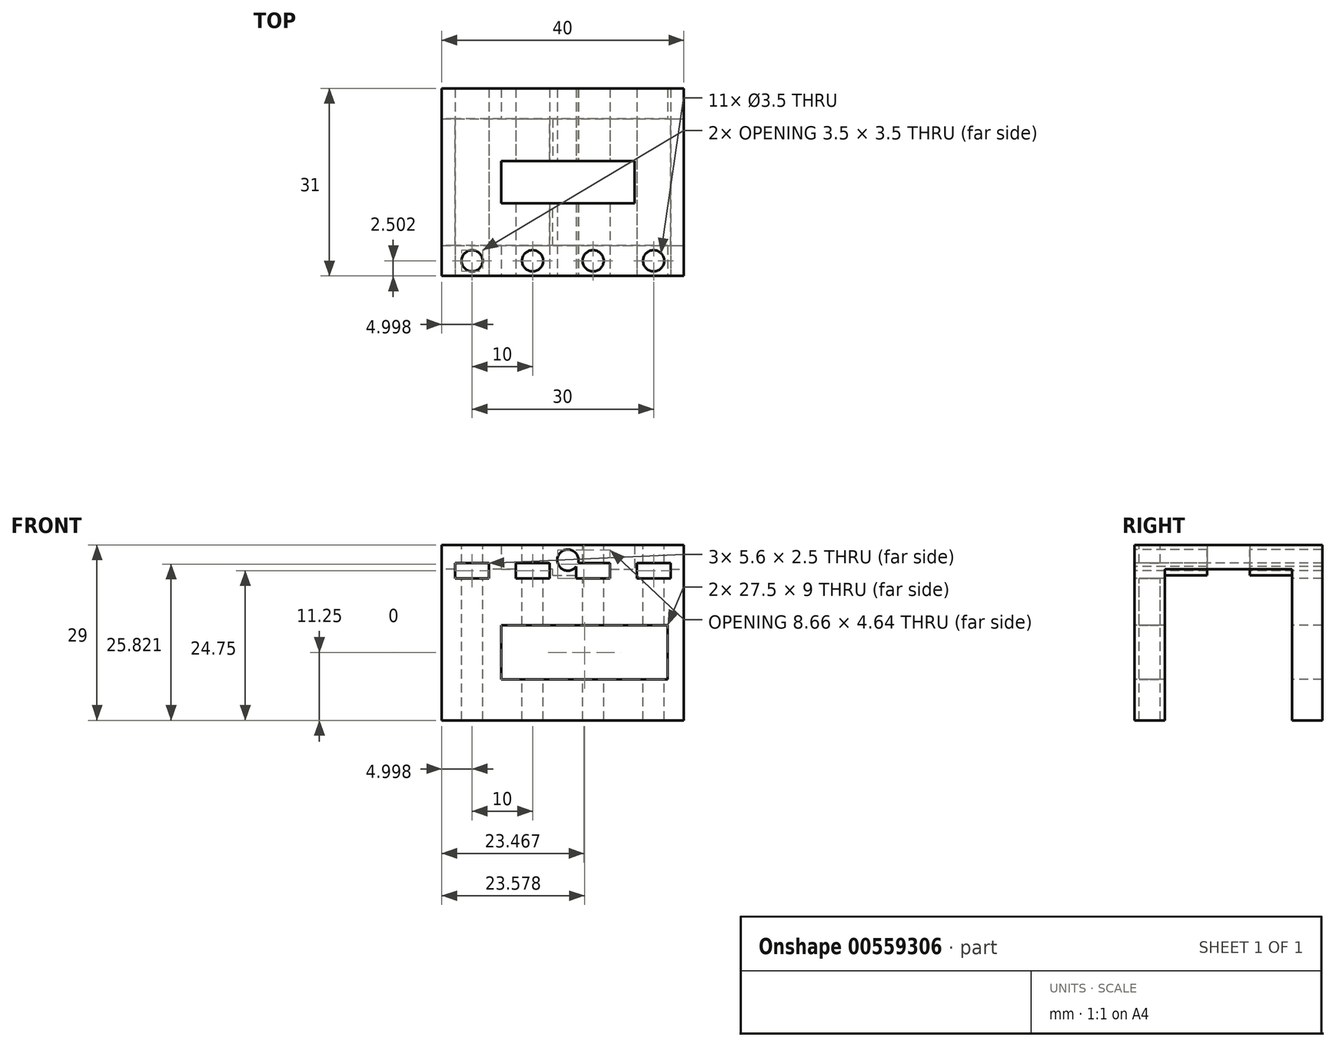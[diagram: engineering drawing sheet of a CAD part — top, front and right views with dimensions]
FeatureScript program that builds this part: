
annotation { "Feature Type Name" : "Feature", "Feature Type Description" : "" }
export const myFeature = defineFeature(function(context is Context, id is Id, definition is map)
    precondition{}
    {
        {
            var Q0;
            Q0=qCreatedBy(makeId("Top.planeOp"),FACE);
            var sketch = newSketch(context, id + "F0", { "sketchPlane" : qUnion([Q0])});
            skLineSegment(sketch, "E0.bottom", {"start": v(-20.38, 4.86) * mm, "end": v(27.96, 4.86) * mm});
            skLineSegment(sketch, "E0.top", {"start": v(-20.38, -15.14) * mm, "end": v(27.96, -15.14) * mm});
            skLineSegment(sketch, "E0.left", {"start": v(-20.38, 4.86) * mm, "end": v(-20.38, -15.14) * mm});
            skLineSegment(sketch, "E0.right", {"start": v(27.96, 4.86) * mm, "end": v(27.96, -15.14) * mm});
            skLineSegment(sketch, "E1.bottom", {"start": v(-7.21, -1.64) * mm, "end": v(14.79, -1.64) * mm});
            skLineSegment(sketch, "E1.top", {"start": v(-7.21, -8.64) * mm, "end": v(14.79, -8.64) * mm});
            skLineSegment(sketch, "E1.left", {"start": v(-7.21, -1.64) * mm, "end": v(-7.21, -8.64) * mm});
            skLineSegment(sketch, "E1.right", {"start": v(14.79, -1.64) * mm, "end": v(14.79, -8.64) * mm});
            skLineSegment(sketch, "E2", {"start": v(3.79, -1.64) * mm, "end": v(3.79, 4.86) * mm, "construction": true});
            skLineSegment(sketch, "E3", {"start": v(3.79, -8.64) * mm, "end": v(3.79, -15.14) * mm, "construction": true});
            skSolve(sketch);
        }
        {
            var Q0;
            Q0=makeQuery(id+"F0.imprint","IMPRINT",FACE,{"disambiguationData":[TD([[makeQuery(id+"F0.imprint","IMPRINT",EDGE,{"derivedFrom":sQuery(id+"F0.wireOp",EDGE,"E0.bottom")}),-1.0]])]});
            extrude(context, id + "F1", {"entities" : qUnion([Q0]), "depth" : 4 * mm, "offsetDistance" : 25 * mm});
        }
        {
            var Q0;
            Q0=makeQuery(id+"F1.opExtrude","CAP_FACE",FACE,{"disambiguationData":[OSD([sQuery(id+"F0.wireOp",EDGE,"E0.bottom"),sQuery(id+"F0.wireOp",EDGE,"E0.top"),sQuery(id+"F0.wireOp",EDGE,"E0.left"),sQuery(id+"F0.wireOp",EDGE,"E0.right"),sQuery(id+"F0.wireOp",EDGE,"E1.bottom"),sQuery(id+"F0.wireOp",EDGE,"E1.top"),sQuery(id+"F0.wireOp",EDGE,"E1.left"),sQuery(id+"F0.wireOp",EDGE,"E1.right")])],"isStart":true});
            var sketch = newSketch(context, id + "F2", { "sketchPlane" : qUnion([Q0])});
            skLineSegment(sketch, "E4", {"start": v(3.79, 8.64) * mm, "end": v(3.79, 1.64) * mm});
            skLineSegment(sketch, "E5", {"start": v(3.79, 8.64) * mm, "end": v(6.29, 8.64) * mm});
            skLineSegment(sketch, "E6", {"start": v(6.29, 8.64) * mm, "end": v(6.29, 15.14) * mm});
            skLineSegment(sketch, "E7", {"start": v(6.29, 15.14) * mm, "end": v(1.29, 15.14) * mm});
            skLineSegment(sketch, "E8", {"start": v(1.29, 15.14) * mm, "end": v(1.29, 8.64) * mm});
            skLineSegment(sketch, "E9", {"start": v(1.29, 8.64) * mm, "end": v(3.79, 8.64) * mm});
            skLineSegment(sketch, "E10", {"start": v(3.79, 1.64) * mm, "end": v(6.29, 1.64) * mm});
            skLineSegment(sketch, "E11", {"start": v(6.29, 1.64) * mm, "end": v(6.29, -4.86) * mm});
            skLineSegment(sketch, "E12", {"start": v(6.29, -4.86) * mm, "end": v(1.29, -4.86) * mm});
            skLineSegment(sketch, "E13", {"start": v(1.29, -4.86) * mm, "end": v(1.29, 1.64) * mm});
            skLineSegment(sketch, "E14", {"start": v(1.29, 1.64) * mm, "end": v(3.79, 1.64) * mm});
            skSolve(sketch);
        }
        {
            var Q0;
            Q0 = qSketchRegion(id + "F2", true);
            extrude(context, id + "F3", {"entities" : qUnion([Q0]), "operationType" : NewBodyOperationType.ADD, "depth" : 1 * mm, "offsetDistance" : 25 * mm});
        }
        {
            var Q0;
            Q0=makeQuery(id+"F3.boolean.opBoolean","MERGE",FACE,{"derivedFrom":[makeQuery(id+"F1.opExtrude","SWEPT_FACE",FACE,{"disambiguationData":[OSD([sQuery(id+"F0.wireOp",EDGE,"E0.top")])]}),makeQuery(id+"F3.opExtrude","SWEPT_FACE",FACE,{"disambiguationData":[OSD([sQuery(id+"F2.wireOp",EDGE,"E7")])]})]});
            var sketch = newSketch(context, id + "F4", { "sketchPlane" : qUnion([Q0])});
            skLineSegment(sketch, "E15", {"start": v(3.79, -1) * mm, "end": v(3.79, 4) * mm, "construction": true});
            skCircle(sketch, "E16", {"center": v(3.79, 1.5) * mm, "radius": 1.75 * mm});
            skSolve(sketch);
        }
        {
            var Q0;
            Q0=makeQuery(id+"F4.imprint","IMPRINT",FACE,{"disambiguationData":[TD([[makeQuery(id+"F4.imprint","IMPRINT",EDGE,{"derivedFrom":sQuery(id+"F4.wireOp",EDGE,"E16")}),1.0]])]});
            extrude(context, id + "F5", {"entities" : qUnion([Q0]), "operationType" : NewBodyOperationType.REMOVE, "endBound" : BoundingType.THROUGH_ALL, "oppositeDirection" : true, "depth" : 25 * mm, "offsetDistance" : 25 * mm});
        }
        {
            var Q0;
            Q0=makeQuery(id+"F3.boolean.opBoolean","MERGE",FACE,{"derivedFrom":[makeQuery(id+"F1.opExtrude","SWEPT_FACE",FACE,{"disambiguationData":[OSD([sQuery(id+"F0.wireOp",EDGE,"E0.top")])]}),makeQuery(id+"F3.opExtrude","SWEPT_FACE",FACE,{"disambiguationData":[OSD([sQuery(id+"F2.wireOp",EDGE,"E7")])]})]});
            extrude(context, id + "F6", {"entities" : qUnion([Q0]), "operationType" : NewBodyOperationType.ADD, "depth" : 5.5 * mm, "offsetDistance" : 25 * mm});
        }
        {
            var Q0;
            Q0=makeQuery(id+"F3.boolean.opBoolean","MERGE",FACE,{"derivedFrom":[makeQuery(id+"F1.opExtrude","SWEPT_FACE",FACE,{"disambiguationData":[OSD([sQuery(id+"F0.wireOp",EDGE,"E0.bottom")])]}),makeQuery(id+"F3.opExtrude","SWEPT_FACE",FACE,{"disambiguationData":[OSD([sQuery(id+"F2.wireOp",EDGE,"E12")])]})]});
            extrude(context, id + "F7", {"entities" : qUnion([Q0]), "operationType" : NewBodyOperationType.ADD, "depth" : 5.5 * mm, "offsetDistance" : 25 * mm});
        }
        {
            var Q0;
            {var subQ1=sQuery(id+"F0.wireOp",EDGE,"E1.right");var subQ2=sQuery(id+"F0.wireOp",EDGE,"E1.top");var subQ3=sQuery(id+"F0.wireOp",EDGE,"E1.bottom");var subQ4=sQuery(id+"F0.wireOp",EDGE,"E0.right");var subQ5=sQuery(id+"F0.wireOp",EDGE,"E0.top");var subQ6=sQuery(id+"F0.wireOp",EDGE,"E0.bottom");var subQ7=makeQuery(id+"F1.opExtrude","CAP_FACE",FACE,{"disambiguationData":[OSD([subQ6,subQ5,sQuery(id+"F0.wireOp",EDGE,"E0.left"),subQ4,subQ3,subQ2,sQuery(id+"F0.wireOp",EDGE,"E1.left"),subQ1])],"isStart":true});var subQ8=makeQuery(id+"F1.opExtrude","SWEPT_FACE",FACE,{"disambiguationData":[OSD([subQ4])]});Q0=makeQuery(id+"F7.boolean.opBoolean","MERGE",FACE,{"derivedFrom":[makeQuery(id+"F6.boolean.opBoolean","MERGE",FACE,{"derivedFrom":[makeQuery(id+"F3.boolean.opBoolean","SPLIT",FACE,{"disambiguationData":[TD([subQ8])],"derivedFrom":subQ7}),makeQuery(id+"F6.opExtrude","SWEPT_FACE",FACE,{"disambiguationData":[OSD([subQ5]),TDD([makeQuery(id+"F3.boolean.opBoolean","SPLIT",EDGE,{"disambiguationData":[TD([subQ8])],"derivedFrom":makeQuery(id+"F1.opExtrude","CAP_EDGE",EDGE,{"disambiguationData":[OSD([subQ5])],"isStart":true})})])]})]}),makeQuery(id+"F7.opExtrude","SWEPT_FACE",FACE,{"disambiguationData":[OSD([subQ6]),TDD([makeQuery(id+"F3.boolean.opBoolean","SPLIT",EDGE,{"disambiguationData":[TD([subQ8])],"derivedFrom":makeQuery(id+"F1.opExtrude","CAP_EDGE",EDGE,{"disambiguationData":[OSD([subQ6])],"isStart":true})})])]})]});}
            var sketch = newSketch(context, id + "F8", { "sketchPlane" : qUnion([Q0])});
            skLineSegment(sketch, "E17.bottom", {"start": v(6.29, -10.36) * mm, "end": v(27.96, -10.36) * mm});
            skLineSegment(sketch, "E17.top", {"start": v(6.29, -5.36) * mm, "end": v(27.96, -5.36) * mm});
            skLineSegment(sketch, "E17.left", {"start": v(6.29, -10.36) * mm, "end": v(6.29, -5.36) * mm});
            skLineSegment(sketch, "E17.right", {"start": v(27.96, -10.36) * mm, "end": v(27.96, -5.36) * mm});
            skLineSegment(sketch, "E18.bottom", {"start": v(6.29, 20.64) * mm, "end": v(27.96, 20.64) * mm});
            skLineSegment(sketch, "E18.top", {"start": v(6.29, 15.64) * mm, "end": v(27.96, 15.64) * mm});
            skLineSegment(sketch, "E18.left", {"start": v(6.29, 20.64) * mm, "end": v(6.29, 15.64) * mm});
            skLineSegment(sketch, "E18.right", {"start": v(27.96, 20.64) * mm, "end": v(27.96, 15.64) * mm});
            skSolve(sketch);
        }
        {
            var Q0;
            Q0 = qSketchRegion(id + "F8", true);
            extrude(context, id + "F9", {"entities" : qUnion([Q0]), "operationType" : NewBodyOperationType.ADD, "depth" : 25 * mm, "offsetDistance" : 25 * mm});
        }
        {
            var Q0;
            {var subQ1=sQuery(id+"F0.wireOp",EDGE,"E0.bottom");var subQ3=sQuery(id+"F0.wireOp",EDGE,"E0.left");var subQ4=makeQuery(id+"F1.opExtrude","SWEPT_FACE",FACE,{"disambiguationData":[OSD([subQ3])]});var subQ5=sQuery(id+"F0.wireOp",EDGE,"E1.left");var subQ6=sQuery(id+"F0.wireOp",EDGE,"E1.top");var subQ7=sQuery(id+"F0.wireOp",EDGE,"E1.bottom");var subQ8=sQuery(id+"F0.wireOp",EDGE,"E0.top");var subQ9=makeQuery(id+"F1.opExtrude","CAP_FACE",FACE,{"disambiguationData":[OSD([subQ1,subQ8,subQ3,sQuery(id+"F0.wireOp",EDGE,"E0.right"),subQ7,subQ6,subQ5,sQuery(id+"F0.wireOp",EDGE,"E1.right")])],"isStart":true});Q0=makeQuery(id+"F7.boolean.opBoolean","MERGE",FACE,{"derivedFrom":[makeQuery(id+"F6.boolean.opBoolean","MERGE",FACE,{"derivedFrom":[makeQuery(id+"F3.boolean.opBoolean","SPLIT",FACE,{"disambiguationData":[TD([subQ4])],"derivedFrom":subQ9}),makeQuery(id+"F6.opExtrude","SWEPT_FACE",FACE,{"disambiguationData":[OSD([subQ8]),TDD([makeQuery(id+"F3.boolean.opBoolean","SPLIT",EDGE,{"disambiguationData":[TD([subQ4])],"derivedFrom":makeQuery(id+"F1.opExtrude","CAP_EDGE",EDGE,{"disambiguationData":[OSD([subQ8])],"isStart":true})})])]})]}),makeQuery(id+"F7.opExtrude","SWEPT_FACE",FACE,{"disambiguationData":[OSD([subQ1]),TDD([makeQuery(id+"F3.boolean.opBoolean","SPLIT",EDGE,{"disambiguationData":[TD([subQ4])],"derivedFrom":makeQuery(id+"F1.opExtrude","CAP_EDGE",EDGE,{"disambiguationData":[OSD([subQ1])],"isStart":true})})])]})]});}
            var sketch = newSketch(context, id + "F10", { "sketchPlane" : qUnion([Q0])});
            skLineSegment(sketch, "E19.bottom", {"start": v(1.29, 20.64) * mm, "end": v(-20.38, 20.64) * mm});
            skLineSegment(sketch, "E19.top", {"start": v(1.29, 15.64) * mm, "end": v(-20.38, 15.64) * mm});
            skLineSegment(sketch, "E19.left", {"start": v(1.29, 20.64) * mm, "end": v(1.29, 15.64) * mm});
            skLineSegment(sketch, "E19.right", {"start": v(-20.38, 20.64) * mm, "end": v(-20.38, 15.64) * mm});
            skLineSegment(sketch, "E20.bottom", {"start": v(1.29, -10.36) * mm, "end": v(-20.38, -10.36) * mm});
            skLineSegment(sketch, "E20.top", {"start": v(1.29, -5.36) * mm, "end": v(-20.38, -5.36) * mm});
            skLineSegment(sketch, "E20.left", {"start": v(1.29, -10.36) * mm, "end": v(1.29, -5.36) * mm});
            skLineSegment(sketch, "E20.right", {"start": v(-20.38, -10.36) * mm, "end": v(-20.38, -5.36) * mm});
            skSolve(sketch);
        }
        {
            var Q0;
            Q0 = qSketchRegion(id + "F10", true);
            extrude(context, id + "F11", {"entities" : qUnion([Q0]), "operationType" : NewBodyOperationType.ADD, "depth" : 25 * mm, "offsetDistance" : 25 * mm});
        }
        {
            var Q0;
            {var subQ0=sQuery(id+"F2.wireOp",EDGE,"E7");Q0=makeQuery(id+"F6.boolean.opBoolean","MERGE",FACE,{"derivedFrom":[makeQuery(id+"F3.opExtrude","CAP_FACE",FACE,{"disambiguationData":[OSD([sQuery(id+"F2.wireOp",EDGE,"E5"),sQuery(id+"F2.wireOp",EDGE,"E6"),subQ0,sQuery(id+"F2.wireOp",EDGE,"E8"),sQuery(id+"F2.wireOp",EDGE,"E9")])],"isStart":false}),makeQuery(id+"F6.opExtrude","SWEPT_FACE",FACE,{"disambiguationData":[OSD([subQ0])]})]});}
            var sketch = newSketch(context, id + "F12", { "sketchPlane" : qUnion([Q0])});
            skLineSegment(sketch, "E21.bottom", {"start": v(6.29, 20.64) * mm, "end": v(1.29, 20.64) * mm});
            skLineSegment(sketch, "E21.top", {"start": v(6.29, 15.64) * mm, "end": v(1.29, 15.64) * mm});
            skLineSegment(sketch, "E21.left", {"start": v(6.29, 20.64) * mm, "end": v(6.29, 15.64) * mm});
            skLineSegment(sketch, "E21.right", {"start": v(1.29, 20.64) * mm, "end": v(1.29, 15.64) * mm});
            skSolve(sketch);
        }
        {
            var Q0;
            Q0 = qSketchRegion(id + "F12", true);
            extrude(context, id + "F13", {"entities" : qUnion([Q0]), "operationType" : NewBodyOperationType.ADD, "depth" : 24 * mm, "offsetDistance" : 25 * mm});
        }
        {
            var Q0;
            {var subQ0=sQuery(id+"F2.wireOp",EDGE,"E12");Q0=makeQuery(id+"F7.boolean.opBoolean","MERGE",FACE,{"derivedFrom":[makeQuery(id+"F3.opExtrude","CAP_FACE",FACE,{"disambiguationData":[OSD([sQuery(id+"F2.wireOp",EDGE,"E10"),sQuery(id+"F2.wireOp",EDGE,"E11"),subQ0,sQuery(id+"F2.wireOp",EDGE,"E13"),sQuery(id+"F2.wireOp",EDGE,"E14")])],"isStart":false}),makeQuery(id+"F7.opExtrude","SWEPT_FACE",FACE,{"disambiguationData":[OSD([subQ0])]})]});}
            var sketch = newSketch(context, id + "F14", { "sketchPlane" : qUnion([Q0])});
            skLineSegment(sketch, "E22.bottom", {"start": v(1.29, -5.36) * mm, "end": v(6.29, -5.36) * mm});
            skLineSegment(sketch, "E22.top", {"start": v(1.29, -10.36) * mm, "end": v(6.29, -10.36) * mm});
            skLineSegment(sketch, "E22.left", {"start": v(1.29, -5.36) * mm, "end": v(1.29, -10.36) * mm});
            skLineSegment(sketch, "E22.right", {"start": v(6.29, -5.36) * mm, "end": v(6.29, -10.36) * mm});
            skSolve(sketch);
        }
        {
            var Q0;
            Q0 = qSketchRegion(id + "F14", true);
            extrude(context, id + "F15", {"entities" : qUnion([Q0]), "operationType" : NewBodyOperationType.ADD, "depth" : 24 * mm, "offsetDistance" : 25 * mm});
        }
        {
            var Q0;
            Q0=makeQuery(id+"F13.boolean.opBoolean","MERGE",FACE,{"derivedFrom":[makeQuery(id+"F11.boolean.opBoolean","MERGE",FACE,{"derivedFrom":[makeQuery(id+"F9.boolean.opBoolean","MERGE",FACE,{"derivedFrom":[makeQuery(id+"F6.opExtrude","CAP_FACE",FACE,{"disambiguationData":[OSD([sQuery(id+"F0.wireOp",EDGE,"E0.top"),sQuery(id+"F2.wireOp",EDGE,"E7")])],"isStart":false}),makeQuery(id+"F9.opExtrude","SWEPT_FACE",FACE,{"disambiguationData":[OSD([sQuery(id+"F8.wireOp",EDGE,"E18.bottom")])]})]}),makeQuery(id+"F11.opExtrude","SWEPT_FACE",FACE,{"disambiguationData":[OSD([sQuery(id+"F10.wireOp",EDGE,"E19.bottom")])]})]}),makeQuery(id+"F13.opExtrude","SWEPT_FACE",FACE,{"disambiguationData":[OSD([sQuery(id+"F12.wireOp",EDGE,"E21.bottom")])]})]});
            var sketch = newSketch(context, id + "F16", { "sketchPlane" : qUnion([Q0])});
            skLineSegment(sketch, "E23", {"start": v(3.79, 1.5) * mm, "end": v(3.79, -8.5) * mm, "construction": true});
            skLineSegment(sketch, "E24", {"start": v(3.79, -8.5) * mm, "end": v(3.79, -13.75) * mm, "construction": true});
            skLineSegment(sketch, "E25", {"start": v(3.79, -13.75) * mm, "end": v(3.79, -18.25) * mm});
            skLineSegment(sketch, "E26", {"start": v(3.79, -18.25) * mm, "end": v(14.79, -18.25) * mm});
            skLineSegment(sketch, "E27", {"start": v(14.79, -18.25) * mm, "end": v(14.79, -9.25) * mm});
            skLineSegment(sketch, "E28", {"start": v(14.79, -9.25) * mm, "end": v(-7.21, -9.25) * mm});
            skLineSegment(sketch, "E29", {"start": v(-7.21, -9.25) * mm, "end": v(-7.21, -18.25) * mm});
            skLineSegment(sketch, "E30", {"start": v(-7.21, -18.25) * mm, "end": v(3.79, -18.25) * mm});
            skLineSegment(sketch, "E31", {"start": v(14.79, -9.25) * mm, "end": v(20.29, -9.25) * mm});
            skLineSegment(sketch, "E32", {"start": v(20.29, -9.25) * mm, "end": v(20.29, -18.25) * mm});
            skLineSegment(sketch, "E33", {"start": v(20.29, -18.25) * mm, "end": v(14.79, -18.25) * mm});
            skLineSegment(sketch, "E34", {"start": v(3.79, -13.75) * mm, "end": v(17.54, -13.75) * mm});
            skPoint(sketch, "E34.endSnap0", {"position": v(17.54, -9.25) * mm});
            skSolve(sketch);
        }
        {
            var Q0;
            Q0 = qSketchRegion(id + "F16", true);
            extrude(context, id + "F17", {"entities" : qUnion([Q0]), "operationType" : NewBodyOperationType.REMOVE, "endBound" : BoundingType.THROUGH_ALL, "oppositeDirection" : true, "depth" : 25 * mm, "offsetDistance" : 25 * mm});
        }
        {
            var Q0;
            {var subQ0=sQuery(id+"F0.wireOp",EDGE,"E0.bottom");var subQ1=sQuery(id+"F0.wireOp",EDGE,"E0.top");Q0=makeQuery(id+"F7.boolean.opBoolean","MERGE",FACE,{"derivedFrom":[makeQuery(id+"F6.boolean.opBoolean","MERGE",FACE,{"derivedFrom":[makeQuery(id+"F1.opExtrude","CAP_FACE",FACE,{"disambiguationData":[OSD([subQ0,subQ1,sQuery(id+"F0.wireOp",EDGE,"E0.left"),sQuery(id+"F0.wireOp",EDGE,"E0.right"),sQuery(id+"F0.wireOp",EDGE,"E1.bottom"),sQuery(id+"F0.wireOp",EDGE,"E1.top"),sQuery(id+"F0.wireOp",EDGE,"E1.left"),sQuery(id+"F0.wireOp",EDGE,"E1.right")])],"isStart":false}),makeQuery(id+"F6.opExtrude","SWEPT_FACE",FACE,{"disambiguationData":[OSD([subQ1]),TDD([makeQuery(id+"F1.opExtrude","CAP_EDGE",EDGE,{"disambiguationData":[OSD([subQ1])],"isStart":false})])]})]}),makeQuery(id+"F7.opExtrude","SWEPT_FACE",FACE,{"disambiguationData":[OSD([subQ0]),TDD([makeQuery(id+"F1.opExtrude","CAP_EDGE",EDGE,{"disambiguationData":[OSD([subQ0])],"isStart":false})])]})]});}
            var sketch = newSketch(context, id + "F18", { "sketchPlane" : qUnion([Q0])});
            skLineSegment(sketch, "E35", {"start": v(27.96, -5.14) * mm, "end": v(-17.04, -5.14) * mm});
            skLineSegment(sketch, "E36", {"start": v(-17.04, -5.14) * mm, "end": v(-17.04, -20.64) * mm});
            skLineSegment(sketch, "E37", {"start": v(-17.04, -20.64) * mm, "end": v(-20.38, -20.64) * mm});
            skLineSegment(sketch, "E38", {"start": v(-20.38, -20.64) * mm, "end": v(-20.38, 10.36) * mm});
            skLineSegment(sketch, "E39", {"start": v(-20.38, 10.36) * mm, "end": v(-17.04, 10.36) * mm});
            skLineSegment(sketch, "E40", {"start": v(-17.04, 10.36) * mm, "end": v(-17.04, -5.14) * mm});
            skLineSegment(sketch, "E41", {"start": v(-12.04, -20.64) * mm, "end": v(-12.04, -18.14) * mm, "construction": true});
            skLineSegment(sketch, "E42", {"start": v(-12.04, -18.14) * mm, "end": v(-17.04, -18.14) * mm, "construction": true});
            skCircle(sketch, "E43", {"center": v(-12.04, -18.14) * mm, "radius": 1.75 * mm});
            skLineSegment(sketch, "E44", {"start": v(-12.04, -18.14) * mm, "end": v(-2.04, -18.14) * mm});
            skLineSegment(sketch, "E45", {"start": v(-2.04, -18.14) * mm, "end": v(7.96, -18.14) * mm});
            skLineSegment(sketch, "E46", {"start": v(7.96, -18.14) * mm, "end": v(17.96, -18.14) * mm});
            skCircle(sketch, "E47", {"center": v(-2.04, -18.14) * mm, "radius": 1.75 * mm});
            skCircle(sketch, "E48", {"center": v(7.96, -18.14) * mm, "radius": 1.75 * mm});
            skCircle(sketch, "E49", {"center": v(17.96, -18.14) * mm, "radius": 1.75 * mm});
            skSolve(sketch);
        }
        {
            var Q0;
            Q0=makeQuery(id+"F18.imprint","IMPRINT",FACE,{"disambiguationData":[TD([[makeQuery(id+"F18.imprint","IMPRINT",EDGE,{"derivedFrom":sQuery(id+"F18.wireOp",EDGE,"E36")}),-1.0]])]});
            extrude(context, id + "F19", {"entities" : qUnion([Q0]), "operationType" : NewBodyOperationType.REMOVE, "endBound" : BoundingType.THROUGH_ALL, "oppositeDirection" : true, "depth" : 25 * mm, "offsetDistance" : 25 * mm});
        }
        {
            var Q0;
            Q0=makeQuery(id+"F18.imprint","IMPRINT",FACE,{"disambiguationData":[TD([[makeQuery(id+"F18.imprint","IMPRINT",EDGE,{"derivedFrom":sQuery(id+"F18.wireOp",EDGE,"E43")}),1.0]])]});
            extrude(context, id + "F20", {"entities" : qUnion([Q0]), "operationType" : NewBodyOperationType.REMOVE, "oppositeDirection" : true, "depth" : 10 * mm, "offsetDistance" : 25 * mm});
        }
        {
            var Q0;
            Q0=makeQuery(id+"F13.boolean.opBoolean","MERGE",FACE,{"derivedFrom":[makeQuery(id+"F11.boolean.opBoolean","MERGE",FACE,{"derivedFrom":[makeQuery(id+"F9.boolean.opBoolean","MERGE",FACE,{"derivedFrom":[makeQuery(id+"F6.opExtrude","CAP_FACE",FACE,{"disambiguationData":[OSD([sQuery(id+"F0.wireOp",EDGE,"E0.top"),sQuery(id+"F2.wireOp",EDGE,"E7")])],"isStart":false}),makeQuery(id+"F9.opExtrude","SWEPT_FACE",FACE,{"disambiguationData":[OSD([sQuery(id+"F8.wireOp",EDGE,"E18.bottom")])]})]}),makeQuery(id+"F11.opExtrude","SWEPT_FACE",FACE,{"disambiguationData":[OSD([sQuery(id+"F10.wireOp",EDGE,"E19.bottom")])]})]}),makeQuery(id+"F13.opExtrude","SWEPT_FACE",FACE,{"disambiguationData":[OSD([sQuery(id+"F12.wireOp",EDGE,"E21.bottom")])]})]});
            var sketch = newSketch(context, id + "F21", { "sketchPlane" : qUnion([Q0])});
            skLineSegment(sketch, "E50", {"start": v(-17.04, 4) * mm, "end": v(-17.04, 1) * mm});
            skLineSegment(sketch, "E51", {"start": v(-17.04, 1) * mm, "end": v(-12.04, 1) * mm});
            skLineSegment(sketch, "E52", {"start": v(-12.04, 1) * mm, "end": v(-9.24, 1) * mm});
            skLineSegment(sketch, "E53", {"start": v(-9.24, 1) * mm, "end": v(-9.24, -1.5) * mm});
            skLineSegment(sketch, "E54", {"start": v(-9.24, -1.5) * mm, "end": v(-14.84, -1.5) * mm});
            skLineSegment(sketch, "E55", {"start": v(-14.84, -1.5) * mm, "end": v(-14.84, 1) * mm});
            skLineSegment(sketch, "E56", {"start": v(22.96, 1) * mm, "end": v(22.96, 4) * mm});
            skLineSegment(sketch, "E57", {"start": v(22.96, 4) * mm, "end": v(27.96, 4) * mm});
            skLineSegment(sketch, "E58", {"start": v(27.96, 4) * mm, "end": v(27.96, -25) * mm});
            skLineSegment(sketch, "E59", {"start": v(27.96, -25) * mm, "end": v(22.96, -25) * mm});
            skLineSegment(sketch, "E60", {"start": v(22.96, -25) * mm, "end": v(22.96, 1) * mm});
            skLineSegment(sketch, "E61", {"start": v(-12.04, 1) * mm, "end": v(-12.04, -1.5) * mm, "construction": true});
            skLineSegment(sketch, "E62", {"start": v(-12.04, -0.25) * mm, "end": v(-7.04, -0.25) * mm, "construction": true});
            skLineSegment(sketch, "E63", {"start": v(-7.04, -0.25) * mm, "end": v(-7.04, -7.32) * mm});
            skLineSegment(sketch, "E64.MirrorCS", {"start": v(-2.04, -0.25) * mm, "end": v(-7.04, -0.25) * mm, "construction": true});
            skLineSegment(sketch, "E65.MirrorCS", {"start": v(-4.84, -1.5) * mm, "end": v(0.76, -1.5) * mm});
            skLineSegment(sketch, "E66.MirrorCS", {"start": v(-4.84, 1) * mm, "end": v(-4.84, -1.5) * mm});
            skLineSegment(sketch, "E67.MirrorCS", {"start": v(-2.04, 1) * mm, "end": v(-2.04, -1.5) * mm, "construction": true});
            skLineSegment(sketch, "E68.MirrorCS", {"start": v(0.76, -1.5) * mm, "end": v(0.76, 1) * mm});
            skLineSegment(sketch, "E69", {"start": v(-4.84, 1) * mm, "end": v(0.76, 1) * mm});
            skLineSegment(sketch, "E70", {"start": v(-2.04, -0.25) * mm, "end": v(2.96, -0.25) * mm, "construction": true});
            skLineSegment(sketch, "E71", {"start": v(2.96, -0.25) * mm, "end": v(2.96, -2.65) * mm});
            skLineSegment(sketch, "E72.MirrorCS", {"start": v(7.96, -0.25) * mm, "end": v(2.96, -0.25) * mm, "construction": true});
            skLineSegment(sketch, "E73.MirrorCS", {"start": v(5.16, -1.5) * mm, "end": v(5.16, 1) * mm});
            skLineSegment(sketch, "E74.MirrorCS", {"start": v(7.96, -0.25) * mm, "end": v(12.96, -0.25) * mm, "construction": true});
            skLineSegment(sketch, "E75.MirrorCS", {"start": v(10.76, 1) * mm, "end": v(5.16, 1) * mm});
            skLineSegment(sketch, "E76.MirrorCS", {"start": v(10.76, 1) * mm, "end": v(10.76, -1.5) * mm});
            skLineSegment(sketch, "E77.MirrorCS", {"start": v(10.76, -1.5) * mm, "end": v(5.16, -1.5) * mm});
            skLineSegment(sketch, "E78.MirrorCS", {"start": v(7.96, 1) * mm, "end": v(7.96, -1.5) * mm, "construction": true});
            skLineSegment(sketch, "E79.MirrorCS", {"start": v(17.96, 1) * mm, "end": v(15.16, 1) * mm});
            skLineSegment(sketch, "E80.MirrorCS", {"start": v(22.96, 1) * mm, "end": v(17.96, 1) * mm});
            skLineSegment(sketch, "E81.MirrorCS", {"start": v(15.16, -1.5) * mm, "end": v(20.76, -1.5) * mm});
            skLineSegment(sketch, "E82.MirrorCS", {"start": v(20.76, -1.5) * mm, "end": v(20.76, 1) * mm});
            skLineSegment(sketch, "E83.MirrorCS", {"start": v(15.16, 1) * mm, "end": v(15.16, -1.5) * mm});
            skLineSegment(sketch, "E84.MirrorCS", {"start": v(17.96, 1) * mm, "end": v(17.96, -1.5) * mm, "construction": true});
            skLineSegment(sketch, "E85.MirrorCS", {"start": v(17.96, -0.25) * mm, "end": v(12.96, -0.25) * mm, "construction": true});
            skSolve(sketch);
        }
        {
            var Q0;
            {var subQ3=sQuery(id+"F21.wireOp",EDGE,"E52");Q0=makeQuery(id+"F21.imprint","IMPRINT",FACE,{"disambiguationData":[TD([[makeQuery(id+"F21.imprint","IMPRINT",EDGE,{"derivedFrom":subQ3}),-1.0]])]});}
            var Q1;
            {var subQ1=sQuery(id+"F21.wireOp",EDGE,"5f7a72da-4a7a-4d33-9aab-1977c549c56c0.MirrorCS");Q1=makeQuery(id+"F21.imprint","IMPRINT",FACE,{"disambiguationData":[TD([[makeQuery(id+"F21.imprint","IMPRINT",EDGE,{"derivedFrom":subQ1}),1.0]])]});}
            var Q2;
            {var subQ1=sQuery(id+"F21.wireOp",EDGE,"e9651bbc-d93a-4db8-b4dc-7c58f14e2e4a3.MirrorCS");Q2=makeQuery(id+"F21.imprint","IMPRINT",FACE,{"disambiguationData":[TD([[makeQuery(id+"F21.imprint","IMPRINT",EDGE,{"derivedFrom":subQ1}),1.0]])]});}
            var Q3;
            {var subQ4=sQuery(id+"F21.wireOp",EDGE,"e9651bbc-d93a-4db8-b4dc-7c58f14e2e4a0.MirrorCS");Q3=makeQuery(id+"F21.imprint","IMPRINT",FACE,{"disambiguationData":[TD([[makeQuery(id+"F21.imprint","IMPRINT",EDGE,{"derivedFrom":subQ4}),1.0]])]});}
            var Q4;
            Q4=makeQuery(id+"F21.imprint","IMPRINT",FACE,{"disambiguationData":[TD([[makeQuery(id+"F21.imprint","IMPRINT",EDGE,{"derivedFrom":sQuery(id+"F21.wireOp",EDGE,"E56")}),-1.0]])]});
            var Q5;
            Q5=makeQuery(id+"F21.imprint","IMPRINT",FACE,{"disambiguationData":[TD([[makeQuery(id+"F21.imprint","IMPRINT",EDGE,{"derivedFrom":sQuery(id+"F21.wireOp",EDGE,"E65.MirrorCS")}),1.0]])]});
            var Q6;
            {var subQ0=sQuery(id+"F21.wireOp",EDGE,"E76.MirrorCS");Q6=makeQuery(id+"F21.imprint","IMPRINT",FACE,{"disambiguationData":[TD([[makeQuery(id+"F21.imprint","IMPRINT",EDGE,{"derivedFrom":subQ0}),-1.0]])]});}
            var Q7;
            {var subQ2=sQuery(id+"F21.wireOp",EDGE,"E79.MirrorCS");Q7=makeQuery(id+"F21.imprint","IMPRINT",FACE,{"disambiguationData":[TD([[makeQuery(id+"F21.imprint","IMPRINT",EDGE,{"derivedFrom":subQ2}),1.0]])]});}
            extrude(context, id + "F22", {"entities" : qUnion([Q0, Q1, Q2, Q3, Q4, Q5, Q6, Q7]), "operationType" : NewBodyOperationType.REMOVE, "endBound" : BoundingType.THROUGH_ALL, "oppositeDirection" : true, "depth" : 25 * mm, "offsetDistance" : 25 * mm});
        }
        {
            var Q0;
            Q0 = qSketchRegion(id + "F18", true);
            extrude(context, id + "F23", {"entities" : qUnion([Q0]), "operationType" : NewBodyOperationType.REMOVE, "endBound" : BoundingType.THROUGH_ALL, "oppositeDirection" : true, "depth" : 25 * mm, "offsetDistance" : 25 * mm});
        }
    });
